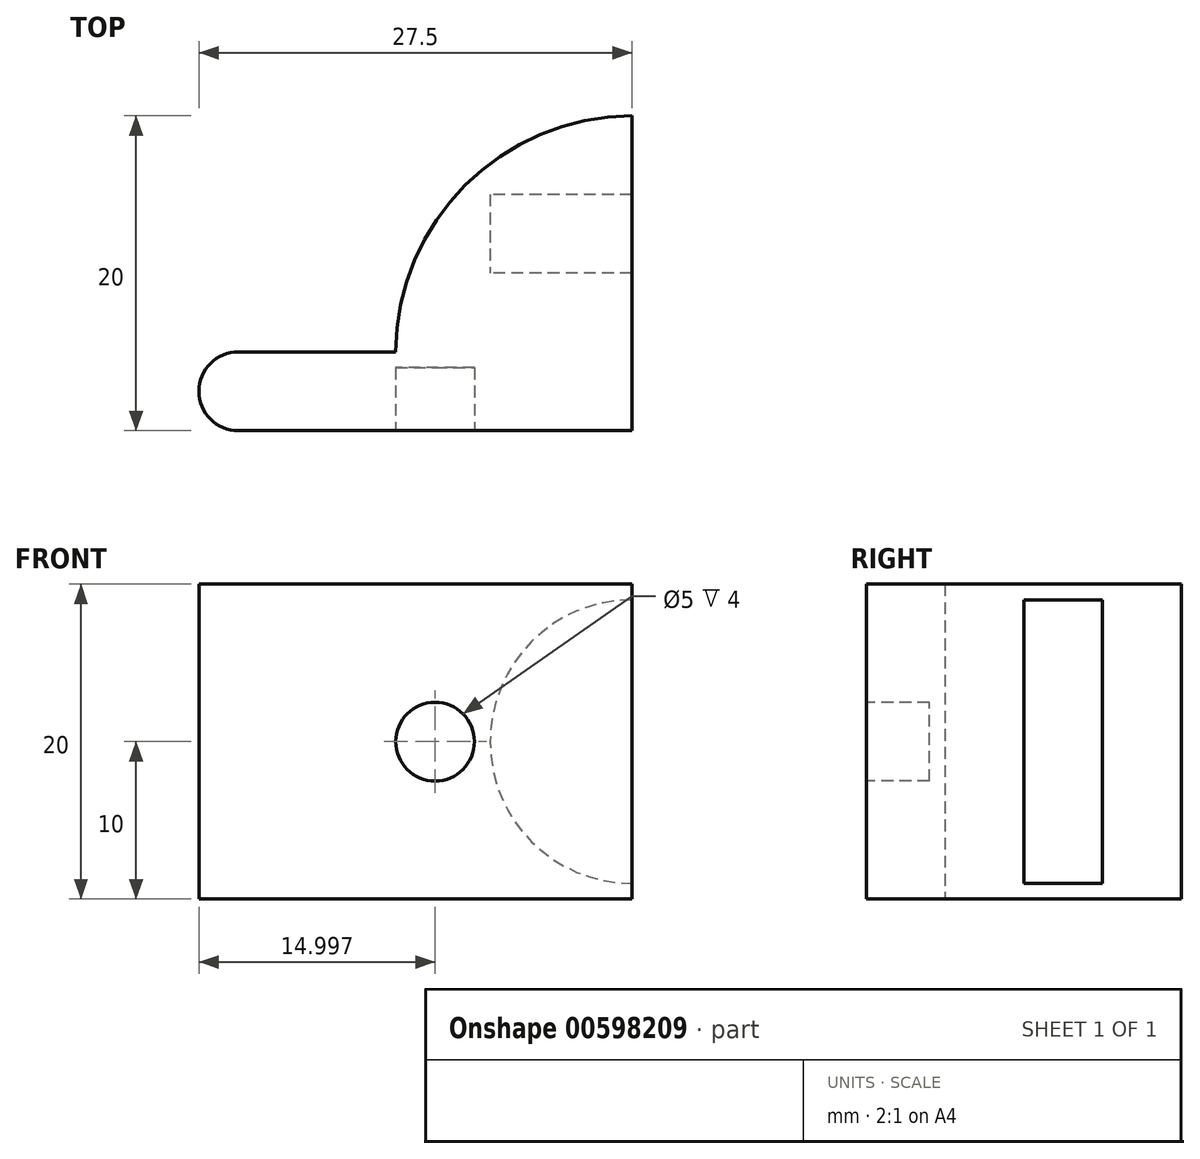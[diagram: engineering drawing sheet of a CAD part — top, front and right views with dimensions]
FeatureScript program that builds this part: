
annotation { "Feature Type Name" : "Feature", "Feature Type Description" : "" }
export const myFeature = defineFeature(function(context is Context, id is Id, definition is map)
    precondition{}
    {
        {
            var Q0;
            Q0=qCreatedBy(makeId("Top.planeOp"),FACE);
            var sketch = newSketch(context, id + "F0", { "sketchPlane" : qUnion([Q0])});
            skLineSegment(sketch, "E0.bottom", {"start": v(-15.83, 4.13) * mm, "end": v(9.17, 4.13) * mm});
            skLineSegment(sketch, "E0.top", {"start": v(-15.83, 9.13) * mm, "end": v(-5.83, 9.13) * mm});
            skLineSegment(sketch, "E1", {"start": v(9.17, 4.13) * mm, "end": v(9.17, 24.13) * mm});
            skArc(sketch, "E2", {"start": v(-15.83, 9.13) * mm, "mid": v(-18.33, 6.63) * mm, "end": v(-15.83, 4.13) * mm});
            skArc(sketch, "E3", {"start": v(9.17, 24.13) * mm, "mid": v(-1.42, 19.72) * mm, "end": v(-5.83, 9.13) * mm});
            skPoint(sketch, "E4.orphan", {"position": v(14.17, 4.13) * mm});
            skSolve(sketch);
        }
        {
            var Q0;
            Q0=makeQuery(id+"F0.imprint","IMPRINT",FACE,{"disambiguationData":[TD([[makeQuery(id+"F0.imprint","IMPRINT",EDGE,{"derivedFrom":sQuery(id+"F0.wireOp",EDGE,"E0.bottom")}),1.0]])]});
            extrude(context, id + "F1", {"entities" : qUnion([Q0]), "depth" : 20 * mm, "offsetDistance" : 25 * mm});
        }
        {
            var Q0;
            Q0=makeQuery(id+"F1.opExtrude","SWEPT_FACE",FACE,{"disambiguationData":[OSD([sQuery(id+"F0.wireOp",EDGE,"E1")])]});
            var sketch = newSketch(context, id + "F2", { "sketchPlane" : qUnion([Q0])});
            skLineSegment(sketch, "E5", {"start": v(19.13, 19) * mm, "end": v(19.13, 10) * mm});
            skLineSegment(sketch, "E6", {"start": v(14.13, 10) * mm, "end": v(19.13, 10) * mm});
            skPoint(sketch, "E6.endSnap0", {"position": v(4.13, 10) * mm});
            skLineSegment(sketch, "E7", {"start": v(14.13, 19) * mm, "end": v(14.13, 10) * mm});
            skPoint(sketch, "E8.orphan", {"position": v(7.18, 10) * mm});
            skLineSegment(sketch, "E9", {"start": v(19.13, 19) * mm, "end": v(14.13, 19) * mm});
            skPoint(sketch, "E10.end.orphan", {"position": v(14.13, 24.76) * mm});
            skPoint(sketch, "E11.end.orphan", {"position": v(19.13, 24.76) * mm});
            skPoint(sketch, "E11.start.orphan", {"position": v(24.13, 20) * mm});
            skLineSegment(sketch, "E12", {"start": v(4.13, 10) * mm, "end": v(-2.64, 10) * mm});
            skSolve(sketch);
        }
        {
            var Q0;
            {var subQ0=sQuery(id+"F2.wireOp",EDGE,"E5");Q0=makeQuery(id+"F2.imprint","IMPRINT",FACE,{"disambiguationData":[TD([[makeQuery(id+"F2.imprint","IMPRINT",EDGE,{"derivedFrom":subQ0}),-1.0]])]});}
            var Q1;
            Q1=sQuery(id+"F2.wireOp",EDGE,"E12");
            revolve(context, id + "F3", {"operationType" : NewBodyOperationType.REMOVE, "entities" : qUnion([Q0]), "axis" : qUnion([Q1]), "revolveType" : RevolveType.FULL, "oppositeDirection" : true});
        }
        {
            var Q0;
            Q0=makeQuery(id+"F1.opExtrude","SWEPT_FACE",FACE,{"disambiguationData":[OSD([sQuery(id+"F0.wireOp",EDGE,"E0.bottom")])]});
            var sketch = newSketch(context, id + "F4", { "sketchPlane" : qUnion([Q0])});
            skPoint(sketch, "E13.endSnap0", {"position": v(-3.33, 20) * mm});
            skCircle(sketch, "E14", {"center": v(-3.33, 10) * mm, "radius": 2.5 * mm});
            skPoint(sketch, "E14.centerSnap0", {"position": v(-3.33, 7.74) * mm});
            skSolve(sketch);
        }
        {
            var Q0;
            Q0=makeQuery(id+"F4.imprint","IMPRINT",FACE,{"disambiguationData":[TD([[makeQuery(id+"F4.imprint","IMPRINT",EDGE,{"derivedFrom":sQuery(id+"F4.wireOp",EDGE,"E14")}),1.0]])]});
            extrude(context, id + "F5", {"entities" : qUnion([Q0]), "operationType" : NewBodyOperationType.REMOVE, "oppositeDirection" : true, "depth" : 4 * mm, "offsetDistance" : 25 * mm});
        }
    });
